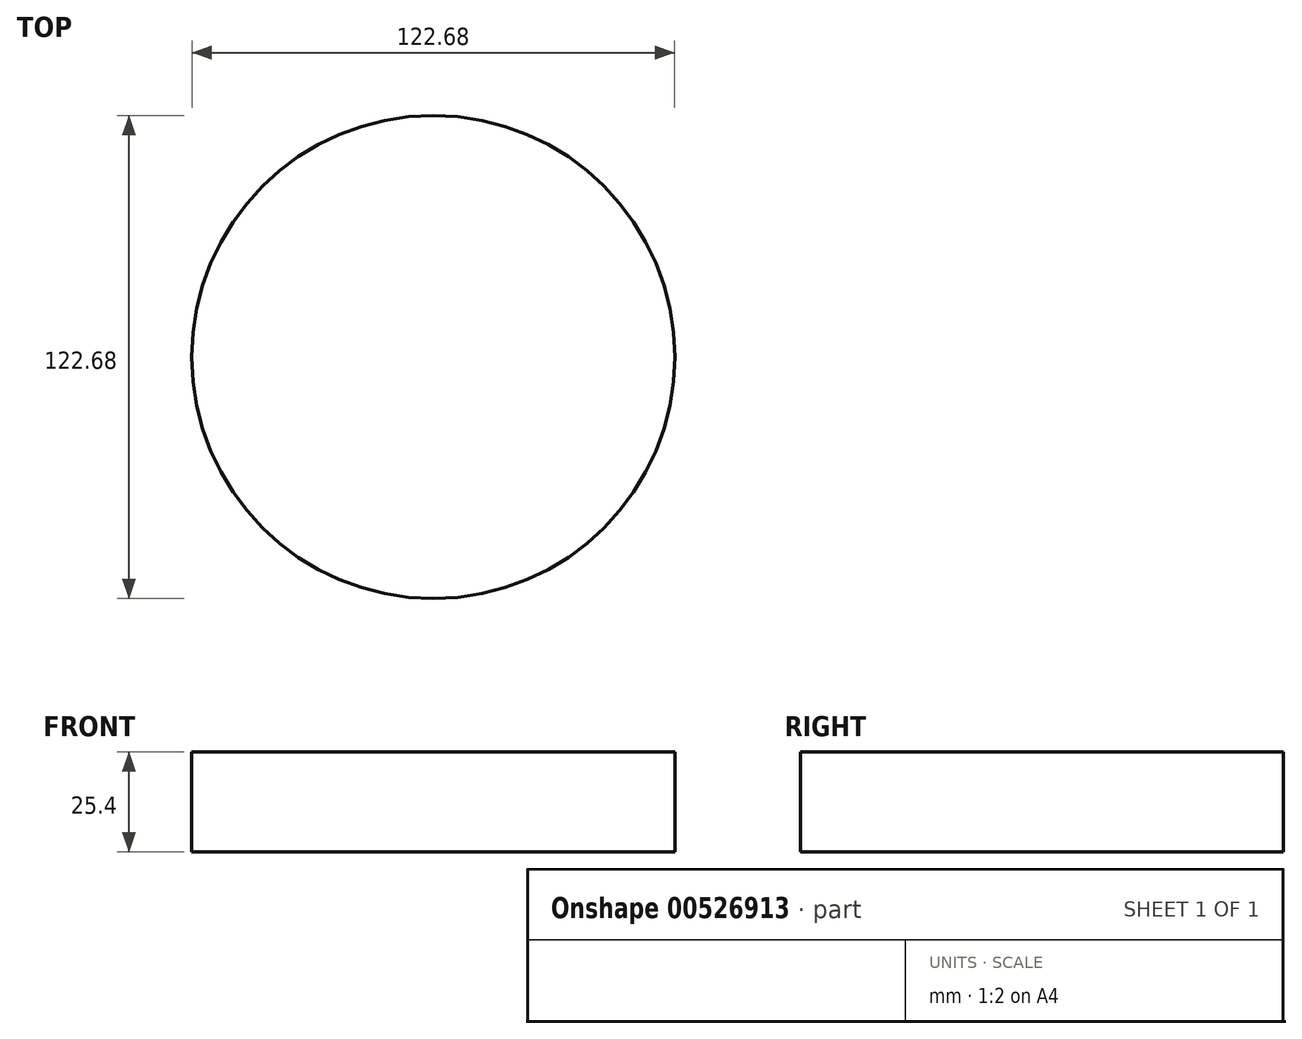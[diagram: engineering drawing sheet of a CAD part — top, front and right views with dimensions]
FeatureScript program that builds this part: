
annotation { "Feature Type Name" : "Feature", "Feature Type Description" : "" }
export const myFeature = defineFeature(function(context is Context, id is Id, definition is map)
    precondition{}
    {
        {
            var Q0;
            Q0=qCreatedBy(makeId("Top.planeOp"),FACE);
            var sketch = newSketch(context, id + "F0", { "sketchPlane" : qUnion([Q0])});
            skCircle(sketch, "E0", {"center": v(-16.83, 9.27) * mm, "radius": 61.34 * mm});
            skSolve(sketch);
        }
        {
            var Q0;
            Q0=makeQuery(id+"F0.imprint","IMPRINT",FACE,{"disambiguationData":[TD([[makeQuery(id+"F0.imprint","IMPRINT",EDGE,{"derivedFrom":sQuery(id+"F0.wireOp",EDGE,"E0")}),1.0]])]});
            extrude(context, id + "F1", {"entities" : qUnion([Q0]), "depth" : 25.4 * mm, "offsetDistance" : 25.4 * mm});
        }
    });
